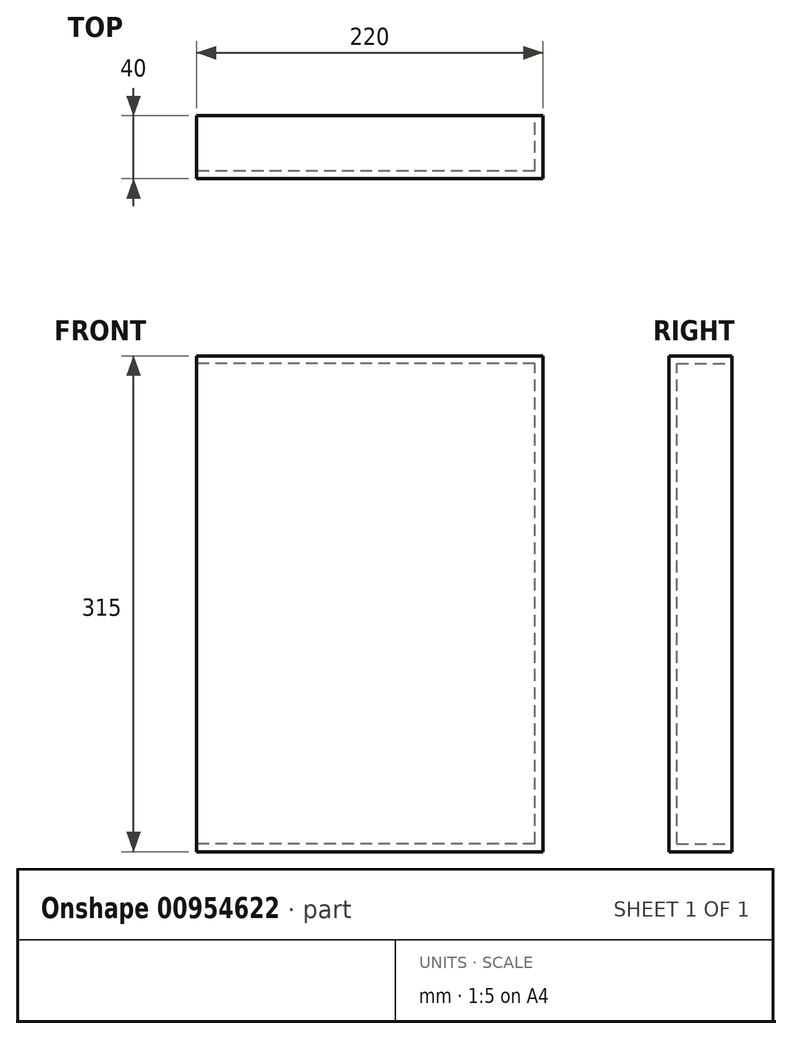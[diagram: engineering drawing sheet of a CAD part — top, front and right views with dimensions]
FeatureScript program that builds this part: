
annotation { "Feature Type Name" : "Feature", "Feature Type Description" : "" }
export const myFeature = defineFeature(function(context is Context, id is Id, definition is map)
    precondition{}
    {
        {
            var Q0;
            Q0=qCreatedBy(makeId("Front.planeOp"),FACE);
            var sketch = newSketch(context, id + "F0", { "sketchPlane" : qUnion([Q0])});
            skLineSegment(sketch, "E0.bottom", {"start": v(110, -157.5) * mm, "end": v(-110, -157.5) * mm});
            skLineSegment(sketch, "E0.top", {"start": v(110, 157.5) * mm, "end": v(-110, 157.5) * mm});
            skLineSegment(sketch, "E0.left", {"start": v(110, -157.5) * mm, "end": v(110, 157.5) * mm});
            skLineSegment(sketch, "E0.right", {"start": v(-110, -157.5) * mm, "end": v(-110, 157.5) * mm, "construction": true});
            skPoint(sketch, "E0.middle", {"position": v(0, 0) * mm});
            skLineSegment(sketch, "E1.0", {"start": v(105, 152.5) * mm, "end": v(-110, 152.5) * mm});
            skLineSegment(sketch, "E1.1", {"start": v(105, -152.5) * mm, "end": v(105, 152.5) * mm});
            skLineSegment(sketch, "E1.2", {"start": v(105, -152.5) * mm, "end": v(-110, -152.5) * mm});
            skLineSegment(sketch, "E2", {"start": v(-110, 157.5) * mm, "end": v(-110, 152.5) * mm});
            skLineSegment(sketch, "E3", {"start": v(-110, -152.5) * mm, "end": v(-110, -157.5) * mm});
            skSolve(sketch);
        }
        {
            var Q0;
            Q0 = qSketchRegion(id + "F0", true);
            extrude(context, id + "F1", {"entities" : qUnion([Q0]), "depth" : 35 * mm, "offsetDistance" : 25 * mm});
        }
        {
            var Q0;
            Q0=makeQuery(id+"F1.opExtrude","CAP_FACE",FACE,{"disambiguationData":[OSD([sQuery(id+"F0.wireOp",EDGE,"E0.bottom"),sQuery(id+"F0.wireOp",EDGE,"E0.top"),sQuery(id+"F0.wireOp",EDGE,"E0.left"),sQuery(id+"F0.wireOp",EDGE,"E1.0"),sQuery(id+"F0.wireOp",EDGE,"E1.1"),sQuery(id+"F0.wireOp",EDGE,"E1.2"),sQuery(id+"F0.wireOp",EDGE,"E2"),sQuery(id+"F0.wireOp",EDGE,"E3")])],"isStart":false});
            var sketch = newSketch(context, id + "F2", { "sketchPlane" : qUnion([Q0])});
            skLineSegment(sketch, "E4.bottom", {"start": v(-110, 157.5) * mm, "end": v(110, 157.5) * mm});
            skLineSegment(sketch, "E4.top", {"start": v(-110, -157.5) * mm, "end": v(110, -157.5) * mm});
            skLineSegment(sketch, "E4.left", {"start": v(-110, 157.5) * mm, "end": v(-110, -157.5) * mm});
            skLineSegment(sketch, "E4.right", {"start": v(110, 157.5) * mm, "end": v(110, -157.5) * mm});
            skSolve(sketch);
        }
        {
            var Q0;
            Q0 = qSketchRegion(id + "F2", true);
            extrude(context, id + "F3", {"entities" : qUnion([Q0]), "operationType" : NewBodyOperationType.ADD, "depth" : 5 * mm, "offsetDistance" : 25 * mm});
        }
    });
